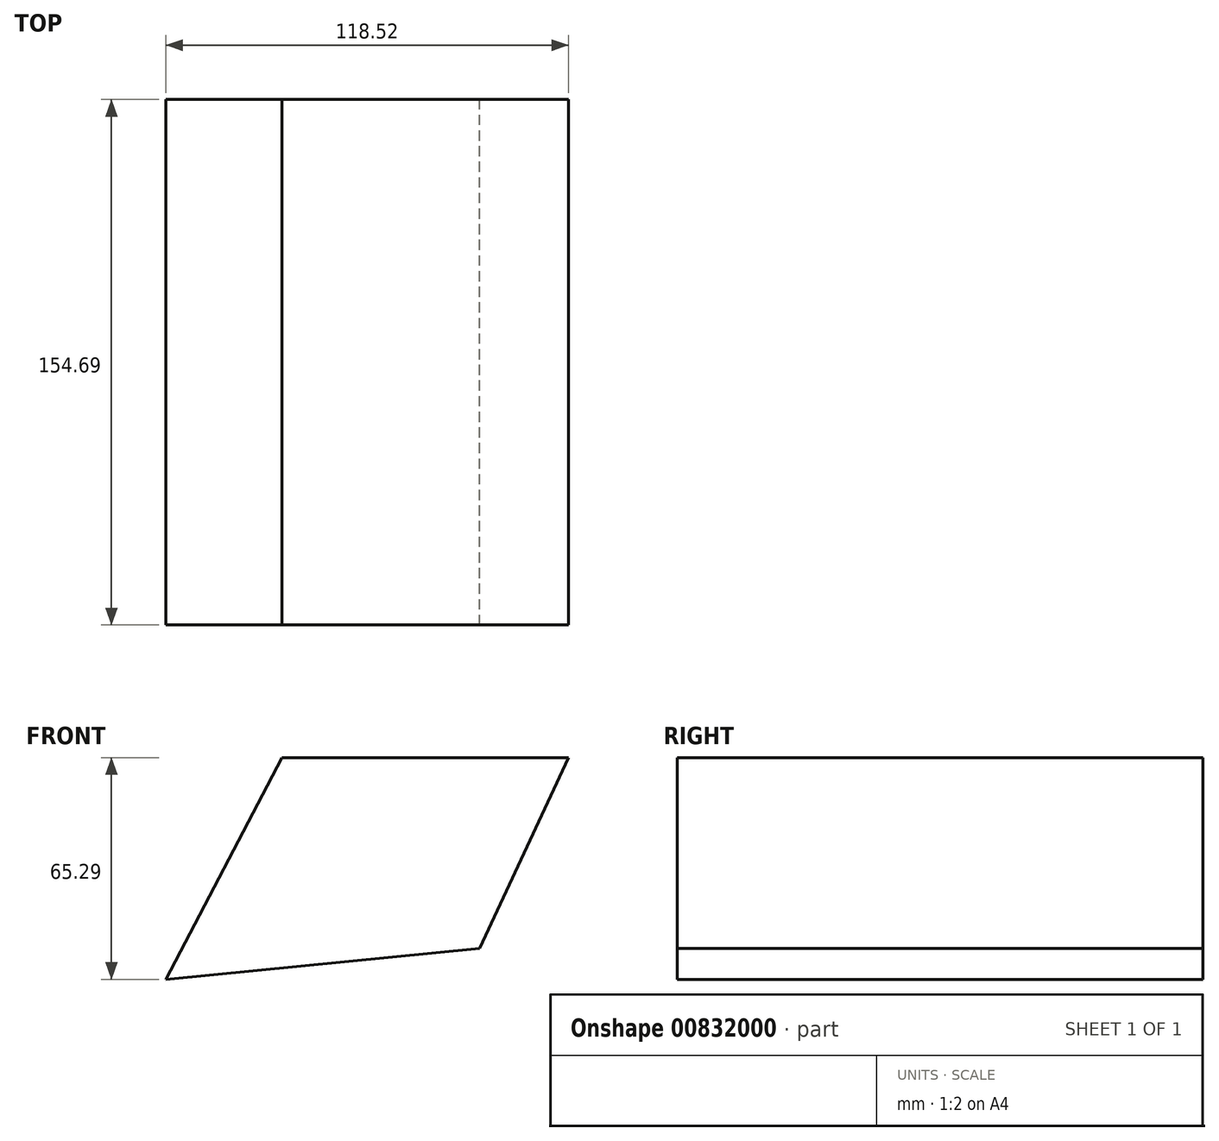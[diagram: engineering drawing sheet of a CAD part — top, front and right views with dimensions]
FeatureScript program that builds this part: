
annotation { "Feature Type Name" : "Feature", "Feature Type Description" : "" }
export const myFeature = defineFeature(function(context is Context, id is Id, definition is map)
    precondition{}
    {
        {
            var Q0;
            Q0=qCreatedBy(makeId("Front.planeOp"),FACE);
            var sketch = newSketch(context, id + "F0", { "sketchPlane" : qUnion([Q0])});
            skLineSegment(sketch, "E0", {"start": v(0, 0) * mm, "end": v(34.18, 65.29) * mm});
            skLineSegment(sketch, "E1", {"start": v(34.18, 65.29) * mm, "end": v(118.52, 65.29) * mm});
            skLineSegment(sketch, "E2", {"start": v(118.52, 65.29) * mm, "end": v(92.4, 9.06) * mm});
            skLineSegment(sketch, "E3", {"start": v(92.4, 9.06) * mm, "end": v(0, 0) * mm});
            skSolve(sketch);
        }
        {
            var Q0;
            Q0 = qSketchRegion(id + "F0", true);
            extrude(context, id + "F1", {"entities" : qUnion([Q0]), "depth" : 154.7 * mm, "offsetDistance" : 25.4 * mm});
        }
    });
